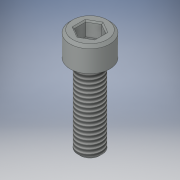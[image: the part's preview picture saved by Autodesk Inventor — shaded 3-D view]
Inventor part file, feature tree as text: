
AUTODESK INVENTOR PART (.ipt)
format: ipt  version: 2017.1 (Build 211199000, 199)  size: 122,368 bytes
history: native  units: in
note: dims shown in document units (in); Inventor stores cm internally (conversion verified against a paired STEP export)
features: thread x1, imported_body x1
ambient origin geometry x8: Origin, YZ Plane, XZ Plane, XY Plane, X Axis, Y Axis, Z Axis, Center Point
bodies: Solid1 (feature_tree)
feature tree (2):
  thread  "Thread1"  [1 undecoded]
  imported_body  "Imported1"
note: 1 required parameter value undecoded (feature->parameter linkage not recoverable at this tier; creation-order binding heuristic only, values carry confidence <= 0.55)
